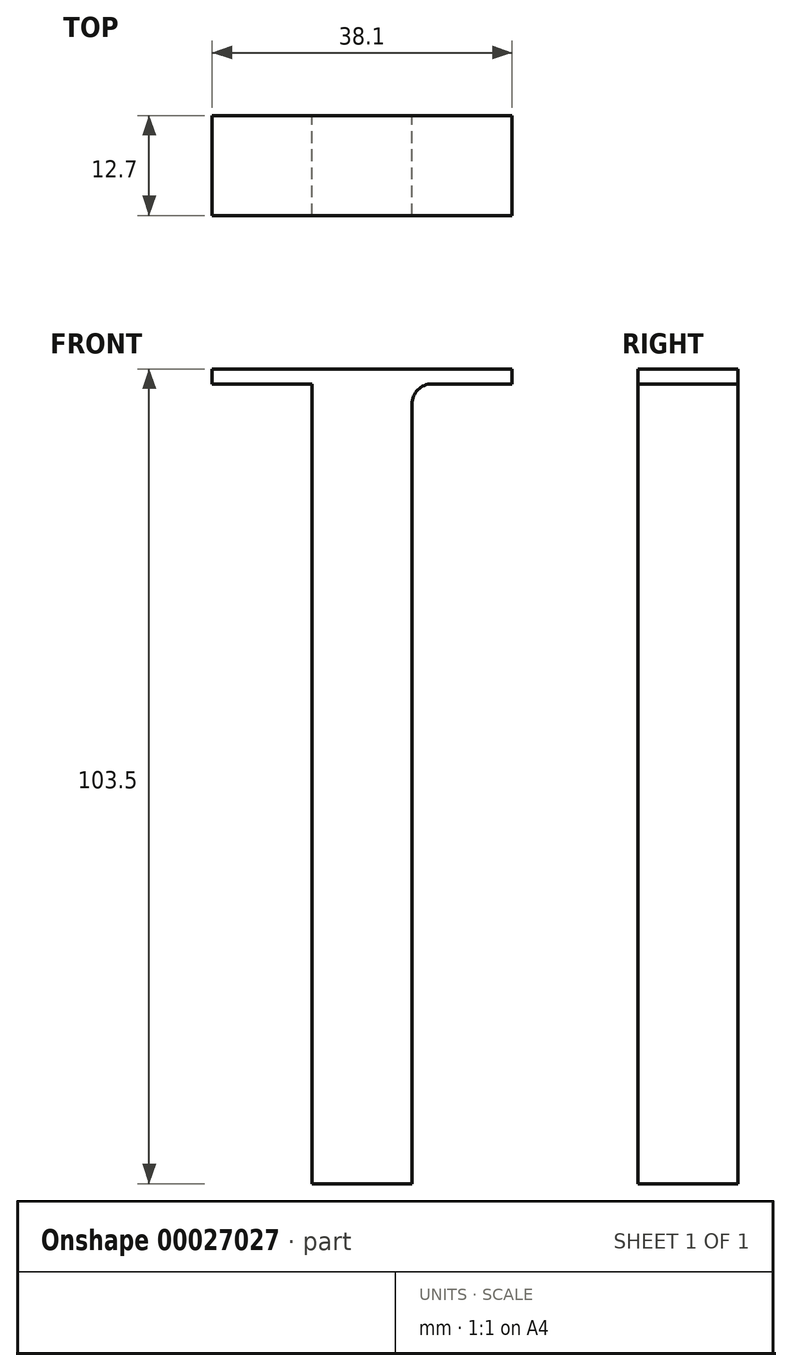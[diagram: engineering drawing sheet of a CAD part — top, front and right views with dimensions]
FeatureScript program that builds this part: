
annotation { "Feature Type Name" : "Feature", "Feature Type Description" : "" }
export const myFeature = defineFeature(function(context is Context, id is Id, definition is map)
    precondition{}
    {
        {
            var Q0;
            Q0=qCreatedBy(makeId("Top.planeOp"),FACE);
            var sketch = newSketch(context, id + "F0", { "sketchPlane" : qUnion([Q0])});
            skLineSegment(sketch, "E0.rect.bottom", {"start": v(6.35, -6.35) * mm, "end": v(-6.35, -6.35) * mm});
            skLineSegment(sketch, "E0.rect.top", {"start": v(6.35, 6.35) * mm, "end": v(-6.35, 6.35) * mm});
            skLineSegment(sketch, "E0.rect.left", {"start": v(6.35, -6.35) * mm, "end": v(6.35, 6.35) * mm});
            skLineSegment(sketch, "E0.rect.right", {"start": v(-6.35, -6.35) * mm, "end": v(-6.35, 6.35) * mm});
            skPoint(sketch, "E0.rect.middle", {"position": v(0, 0) * mm});
            skSolve(sketch);
        }
        {
            var Q0;
            Q0 = qSketchRegion(id + "F0", true);
            extrude(context, id + "F1", {"entities" : qUnion([Q0]), "depth" : 101.6 * mm});
        }
        {
            var Q0;
            Q0=makeQuery(id+"F1.opExtrude","CAP_FACE",FACE,{"disambiguationData":[OSD([sQuery(id+"F0.wireOp",EDGE,"E0.rect.bottom"),sQuery(id+"F0.wireOp",EDGE,"E0.rect.top"),sQuery(id+"F0.wireOp",EDGE,"E0.rect.left"),sQuery(id+"F0.wireOp",EDGE,"E0.rect.right")])],"isStart":false});
            var sketch = newSketch(context, id + "F2", { "sketchPlane" : qUnion([Q0])});
            skLineSegment(sketch, "E1.rect.bottom", {"start": v(-19.05, -6.35) * mm, "end": v(19.05, -6.35) * mm});
            skLineSegment(sketch, "E1.rect.top", {"start": v(-19.05, 6.35) * mm, "end": v(19.05, 6.35) * mm});
            skLineSegment(sketch, "E1.rect.left", {"start": v(-19.05, -6.35) * mm, "end": v(-19.05, 6.35) * mm});
            skLineSegment(sketch, "E1.rect.right", {"start": v(19.05, -6.35) * mm, "end": v(19.05, 6.35) * mm});
            skPoint(sketch, "E1.rect.middle", {"position": v(0, 0) * mm});
            skSolve(sketch);
        }
        {
            var Q0;
            Q0 = qSketchRegion(id + "F2", true);
            extrude(context, id + "F3", {"entities" : qUnion([Q0]), "operationType" : NewBodyOperationType.ADD, "depth" : 1.9 * mm});
        }
        {
            var Q0;
            Q0=makeQuery(id+"F1.opExtrude","CAP_EDGE",EDGE,{"disambiguationData":[OSD([sQuery(id+"F0.wireOp",EDGE,"E0.rect.left")])],"isStart":false});
            var Q1;
            Q1=makeQuery(id+"F1.opExtrude","CAP_EDGE",EDGE,{"disambiguationData":[OSD([sQuery(id+"F0.wireOp",EDGE,"E0.rect.right")])],"isStart":false});
            fillet(context, id + "F4", {"entities" : qUnion([Q0, Q1]), "radius" : 2.54 * mm, "tangentPropagation" : true, "allowEdgeOverflow" : false});
        }
    });
